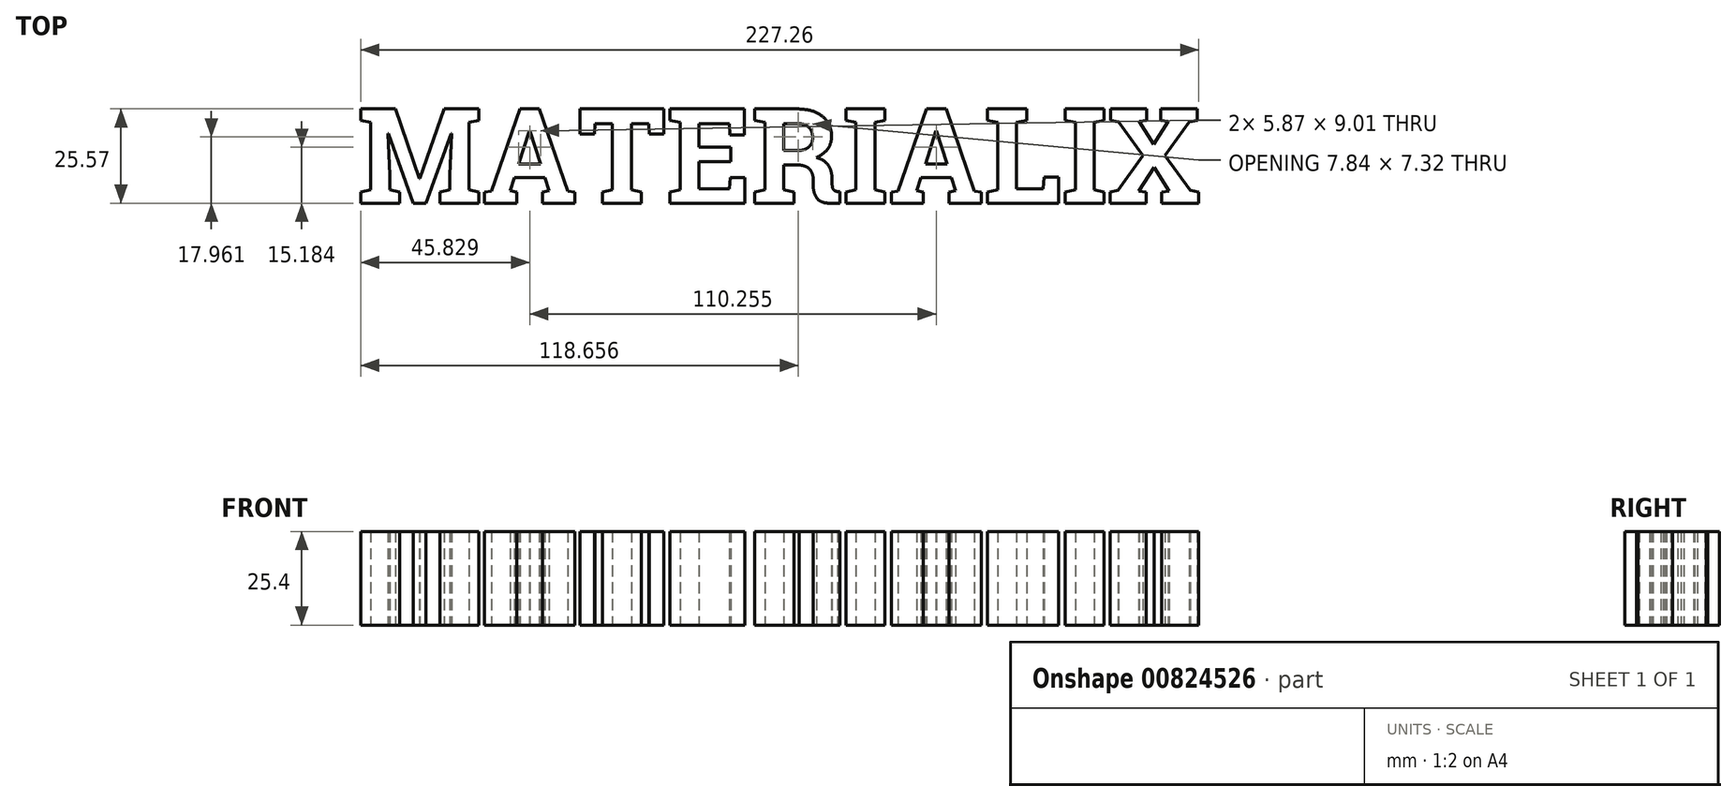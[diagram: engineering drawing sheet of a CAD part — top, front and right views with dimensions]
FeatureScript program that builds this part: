
annotation { "Feature Type Name" : "Feature", "Feature Type Description" : "" }
export const myFeature = defineFeature(function(context is Context, id is Id, definition is map)
    precondition{}
    {
        {
            var Q0;
            Q0=qCreatedBy(makeId("Top.planeOp"),FACE);
            var sketch = newSketch(context, id + "F0", { "sketchPlane" : qUnion([Q0])});
            skText(sketch, "E0", { "text": "MATERIALIX", "fontName": "RobotoSlab-Bold.ttf"});
            const initialGuessF0  = {"E0": [-0.04656, -0.02233, 1, 0, 0.0259]};
            skSetInitialGuess(sketch, initialGuessF0);
            skSolve(sketch);
        }
        {
            var Q0;
            Q0 = qSketchRegion(id + "F0", true);
            extrude(context, id + "F1", {"entities" : qUnion([Q0]), "depth" : 25.4 * mm, "offsetDistance" : 25.4 * mm});
        }
    });
